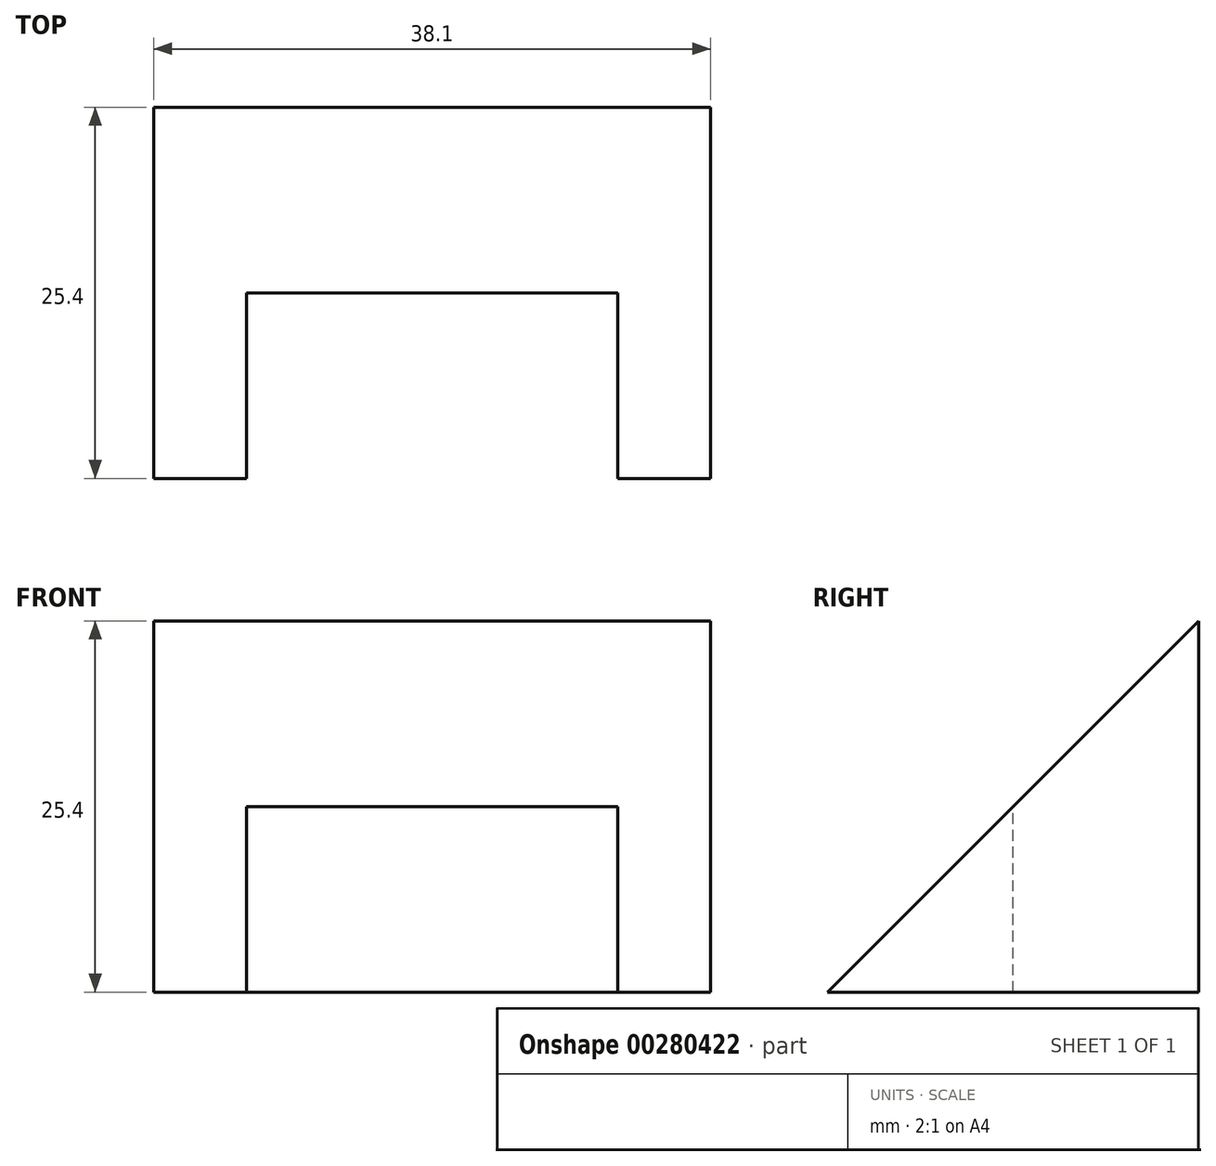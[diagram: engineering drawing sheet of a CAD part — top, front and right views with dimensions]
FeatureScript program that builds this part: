
annotation { "Feature Type Name" : "Feature", "Feature Type Description" : "" }
export const myFeature = defineFeature(function(context is Context, id is Id, definition is map)
    precondition{}
    {
        {
            var Q0;
            Q0=qCreatedBy(makeId("Right.planeOp"),FACE);
            var sketch = newSketch(context, id + "F0", { "sketchPlane" : qUnion([Q0])});
            skLineSegment(sketch, "E0", {"start": v(0, 0) * mm, "end": v(0, 25.4) * mm});
            skLineSegment(sketch, "E1", {"start": v(0, 25.4) * mm, "end": v(-25.4, 0) * mm});
            skLineSegment(sketch, "E2", {"start": v(-25.4, 0) * mm, "end": v(0, 0) * mm});
            skSolve(sketch);
        }
        {
            var Q0;
            Q0 = qSketchRegion(id + "F0", true);
            extrude(context, id + "F1", {"entities" : qUnion([Q0]), "depth" : 38.1 * mm, "symmetric" : true});
        }
        {
            var Q0;
            Q0=qCreatedBy(makeId("Right.planeOp"),FACE);
            var sketch = newSketch(context, id + "F2", { "sketchPlane" : qUnion([Q0])});
            skLineSegment(sketch, "E3", {"start": v(-25.4, 0) * mm, "end": v(-12.7, 0) * mm});
            skLineSegment(sketch, "E4", {"start": v(-12.7, 0) * mm, "end": v(-12.7, 12.7) * mm});
            skLineSegment(sketch, "E5", {"start": v(-12.7, 12.7) * mm, "end": v(-25.4, 0) * mm});
            skSolve(sketch);
        }
        {
            var Q0;
            Q0 = qSketchRegion(id + "F2", true);
            extrude(context, id + "F3", {"entities" : qUnion([Q0]), "operationType" : NewBodyOperationType.REMOVE, "oppositeDirection" : true, "depth" : 25.4 * mm, "symmetric" : true});
        }
    });
